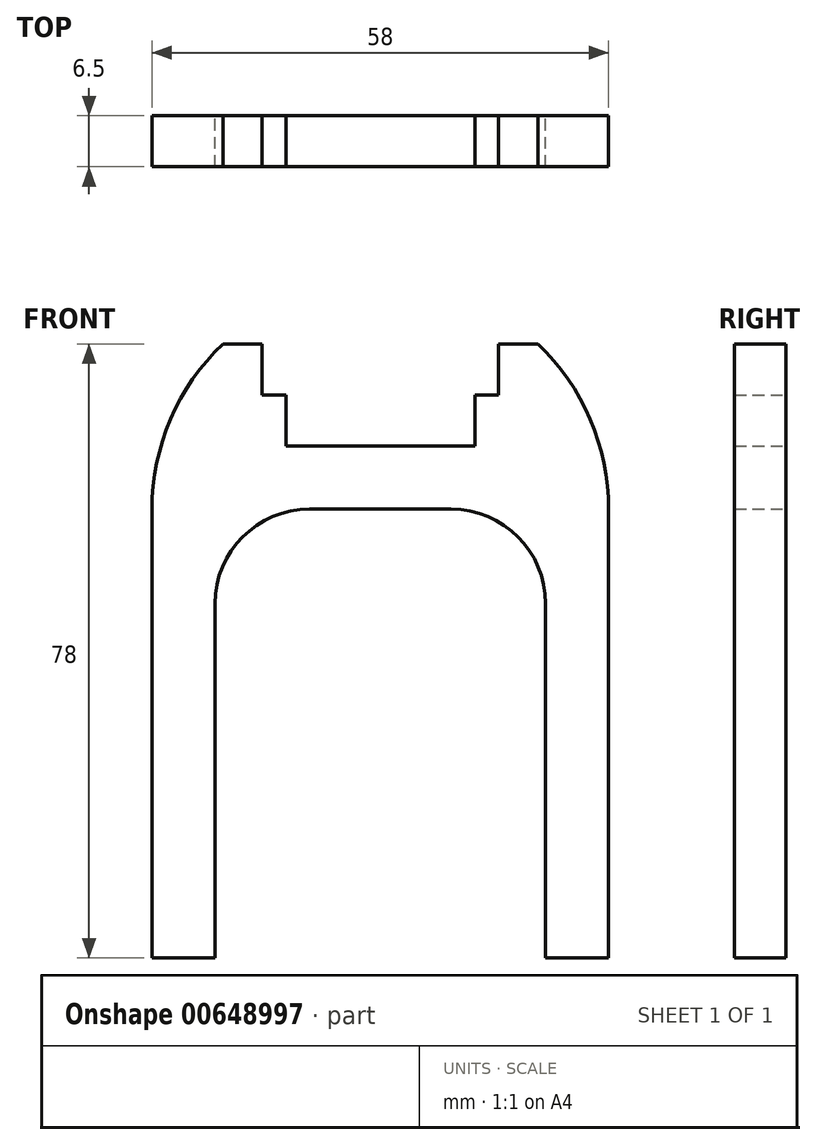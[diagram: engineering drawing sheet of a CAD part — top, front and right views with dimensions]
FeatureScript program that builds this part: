
annotation { "Feature Type Name" : "Feature", "Feature Type Description" : "" }
export const myFeature = defineFeature(function(context is Context, id is Id, definition is map)
    precondition{}
    {
        {
            var Q0;
            Q0=qCreatedBy(makeId("Front.planeOp"),FACE);
            var sketch = newSketch(context, id + "F0", { "sketchPlane" : qUnion([Q0])});
            skLineSegment(sketch, "E0", {"start": v(12, 0) * mm, "end": v(-12, 0) * mm});
            skLineSegment(sketch, "E1", {"start": v(-12, 0) * mm, "end": v(-12, 6.5) * mm});
            skLineSegment(sketch, "E2", {"start": v(-12, 6.5) * mm, "end": v(-15, 6.5) * mm});
            skLineSegment(sketch, "E3", {"start": v(-15, 6.5) * mm, "end": v(-15, 13) * mm});
            skLineSegment(sketch, "E4", {"start": v(-15, 13) * mm, "end": v(-20, 13) * mm});
            skLineSegment(sketch, "E5", {"start": v(12, 0) * mm, "end": v(12, 6.5) * mm});
            skLineSegment(sketch, "E6", {"start": v(12, 6.5) * mm, "end": v(15, 6.5) * mm});
            skLineSegment(sketch, "E7", {"start": v(15, 6.5) * mm, "end": v(15, 13) * mm});
            skLineSegment(sketch, "E8", {"start": v(15, 13) * mm, "end": v(20, 13) * mm});
            skLineSegment(sketch, "E9", {"start": v(-29, -8) * mm, "end": v(-29, -65) * mm});
            skLineSegment(sketch, "E10", {"start": v(-29, -65) * mm, "end": v(-21, -65) * mm});
            skLineSegment(sketch, "E11", {"start": v(-21, -65) * mm, "end": v(-21, -20) * mm});
            skLineSegment(sketch, "E12", {"start": v(-9, -8) * mm, "end": v(9, -8) * mm});
            skLineSegment(sketch, "E13", {"start": v(21, -20) * mm, "end": v(21, -65) * mm});
            skLineSegment(sketch, "E14", {"start": v(21, -65) * mm, "end": v(29, -65) * mm});
            skLineSegment(sketch, "E15", {"start": v(29, -65) * mm, "end": v(29, -8) * mm});
            skArc(sketch, "E16", {"start": v(-29, -8) * mm, "mid": v(-26.66, 3.42) * mm, "end": v(-20, 13) * mm});
            skArc(sketch, "E17", {"start": v(29, -8) * mm, "mid": v(26.66, 3.42) * mm, "end": v(20, 13) * mm});
            skPoint(sketch, "E18.visualSharp", {"position": v(-21, -8) * mm});
            skArc(sketch, "E18.filletArc", {"start": v(-9, -8) * mm, "mid": v(-17.49, -11.51) * mm, "end": v(-21, -20) * mm});
            skPoint(sketch, "E19.visualSharp", {"position": v(21, -8) * mm});
            skArc(sketch, "E19.filletArc", {"start": v(21, -20) * mm, "mid": v(17.49, -11.51) * mm, "end": v(9, -8) * mm});
            skSolve(sketch);
        }
        {
            var Q0;
            Q0=makeQuery(id+"F0.imprint","IMPRINT",FACE,{"disambiguationData":[TD([[makeQuery(id+"F0.imprint","IMPRINT",EDGE,{"derivedFrom":sQuery(id+"F0.wireOp",EDGE,"E0")}),1.0]])]});
            extrude(context, id + "F1", {"entities" : qUnion([Q0]), "endBound" : BoundingType.SYMMETRIC, "depth" : 6.5 * mm, "offsetDistance" : 25 * mm});
        }
    });
